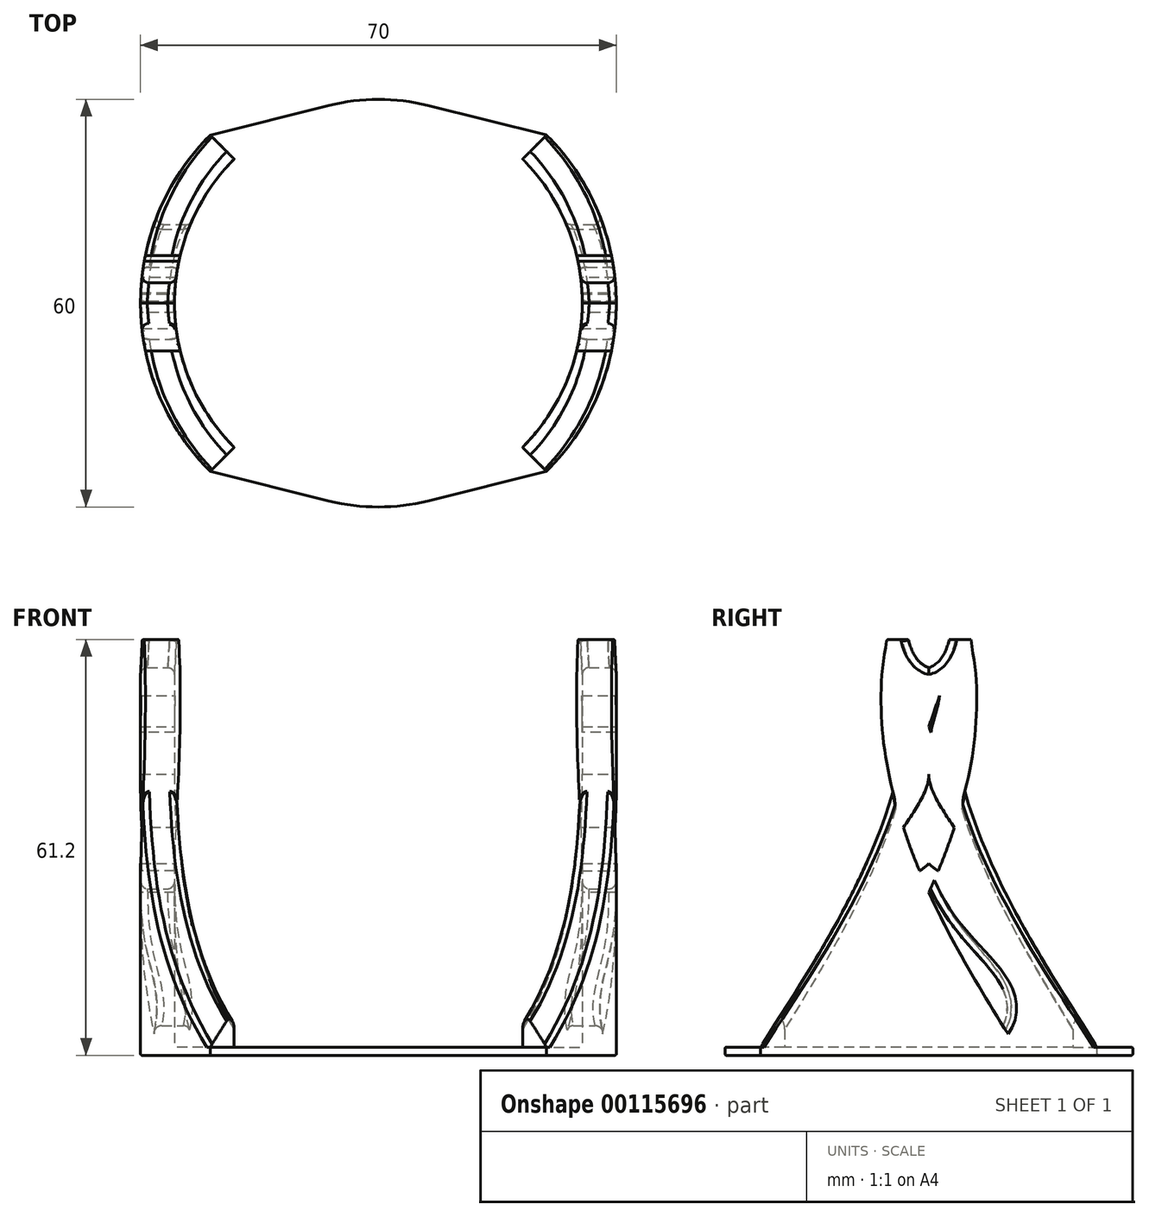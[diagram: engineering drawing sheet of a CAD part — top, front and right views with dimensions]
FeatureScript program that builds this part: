
annotation { "Feature Type Name" : "Feature", "Feature Type Description" : "" }
export const myFeature = defineFeature(function(context is Context, id is Id, definition is map)
    precondition{}
    {
        {
            var Q0;
            Q0=qCreatedBy(makeId("Top.planeOp"),FACE);
            var sketch = newSketch(context, id + "F0", { "sketchPlane" : qUnion([Q0])});
            skCircle(sketch, "E0", {"center": v(0, 0) * mm, "radius": 30 * mm});
            skArc(sketch, "E1", {"start": v(-24.75, 24.75) * mm, "mid": v(-35, 0) * mm, "end": v(-24.75, -24.75) * mm});
            skLineSegment(sketch, "E2", {"start": v(-21.21, 21.21) * mm, "end": v(-24.75, 24.75) * mm});
            skLineSegment(sketch, "E3.MirrorCS", {"start": v(-21.21, -21.21) * mm, "end": v(-24.75, -24.75) * mm});
            skLineSegment(sketch, "E4.MirrorCS", {"start": v(21.21, 21.21) * mm, "end": v(24.75, 24.75) * mm});
            skLineSegment(sketch, "E5.MirrorCS", {"start": v(21.21, -21.21) * mm, "end": v(24.75, -24.75) * mm});
            skArc(sketch, "E6.trimOffspring", {"start": v(24.75, -24.75) * mm, "mid": v(35, 0) * mm, "end": v(24.75, 24.75) * mm});
            skPoint(sketch, "E7.start.orphan", {"position": v(-35, 0) * mm});
            skLineSegment(sketch, "E8", {"start": v(-24.75, 24.75) * mm, "end": v(-7.26, 29.1) * mm});
            skLineSegment(sketch, "E9.MirrorCS", {"start": v(-24.75, -24.75) * mm, "end": v(-7.26, -29.1) * mm});
            skLineSegment(sketch, "E10.MirrorCS", {"start": v(24.75, 24.75) * mm, "end": v(7.26, 29.1) * mm});
            skLineSegment(sketch, "E11.MirrorCS", {"start": v(24.75, -24.75) * mm, "end": v(7.26, -29.1) * mm});
            skSolve(sketch);
        }
        {
            var Q0;
            {var subQ0=sQuery(id+"F0.wireOp",EDGE,"E0");var subQ1=makeQuery(id+"F0.imprint","INTERSECT",VERTEX,{"derivedFrom":[subQ0,sQuery(id+"F0.wireOp",EDGE,"E2")]});Q0=makeQuery(id+"F0.imprint","IMPRINT",FACE,{"disambiguationData":[TD([[makeQuery(id+"F0.imprint","IMPRINT",EDGE,{"disambiguationData":[TD([[subQ1,1.0]])],"derivedFrom":subQ0}),1.0]])]});}
            var Q1;
            {var subQ0=sQuery(id+"F0.wireOp",EDGE,"E2");Q1=makeQuery(id+"F0.imprint","IMPRINT",FACE,{"disambiguationData":[TD([[makeQuery(id+"F0.imprint","IMPRINT",EDGE,{"derivedFrom":subQ0}),-1.0]])]});}
            var Q2;
            {var subQ0=sQuery(id+"F0.wireOp",EDGE,"E4.MirrorCS");Q2=makeQuery(id+"F0.imprint","IMPRINT",FACE,{"disambiguationData":[TD([[makeQuery(id+"F0.imprint","IMPRINT",EDGE,{"derivedFrom":subQ0}),1.0]])]});}
            var Q3;
            {var subQ0=sQuery(id+"F0.wireOp",EDGE,"E5.MirrorCS");Q3=makeQuery(id+"F0.imprint","IMPRINT",FACE,{"disambiguationData":[TD([[makeQuery(id+"F0.imprint","IMPRINT",EDGE,{"derivedFrom":subQ0}),-1.0]])]});}
            var Q4;
            {var subQ0=sQuery(id+"F0.wireOp",EDGE,"E3.MirrorCS");Q4=makeQuery(id+"F0.imprint","IMPRINT",FACE,{"disambiguationData":[TD([[makeQuery(id+"F0.imprint","IMPRINT",EDGE,{"derivedFrom":subQ0}),1.0]])]});}
            extrude(context, id + "F1", {"entities" : qUnion([Q0, Q1, Q2, Q3, Q4]), "oppositeDirection" : true, "depth" : 1.2 * mm});
        }
        {
            var Q0;
            Q0=makeQuery(id+"F0.imprint","IMPRINT",FACE,{"disambiguationData":[TD([[makeQuery(id+"F0.imprint","IMPRINT",EDGE,{"derivedFrom":sQuery(id+"F0.wireOp",EDGE,"E1")}),1.0]])]});
            var Q1;
            {var subQ0=sQuery(id+"F0.wireOp",EDGE,"E4.MirrorCS");Q1=makeQuery(id+"F0.imprint","IMPRINT",FACE,{"disambiguationData":[TD([[makeQuery(id+"F0.imprint","IMPRINT",EDGE,{"derivedFrom":subQ0}),-1.0]])]});}
            extrude(context, id + "F2", {"entities" : qUnion([Q0, Q1]), "operationType" : NewBodyOperationType.ADD, "oppositeDirection" : true, "depth" : 1.2 * mm});
        }
        {
            var Q0;
            Q0=makeQuery(id+"F0.imprint","IMPRINT",FACE,{"disambiguationData":[TD([[makeQuery(id+"F0.imprint","IMPRINT",EDGE,{"derivedFrom":sQuery(id+"F0.wireOp",EDGE,"E1")}),1.0]])]});
            var Q1;
            {var subQ0=sQuery(id+"F0.wireOp",EDGE,"E4.MirrorCS");Q1=makeQuery(id+"F0.imprint","IMPRINT",FACE,{"disambiguationData":[TD([[makeQuery(id+"F0.imprint","IMPRINT",EDGE,{"derivedFrom":subQ0}),-1.0]])]});}
            extrude(context, id + "F3", {"entities" : qUnion([Q0, Q1]), "operationType" : NewBodyOperationType.ADD, "depth" : 60 * mm});
        }
        {
            var Q0;
            Q0=qCreatedBy(makeId("Right.planeOp"),FACE);
            var sketch = newSketch(context, id + "F4", { "sketchPlane" : qUnion([Q0])});
            skLineSegment(sketch, "E12.0", {"start": v(24.75, 60) * mm, "end": v(-24.75, 60) * mm});
            skLineSegment(sketch, "E13.0", {"start": v(24.75, 60) * mm, "end": v(24.75, 0) * mm});
            skLineSegment(sketch, "E14.0", {"start": v(-24.75, 60) * mm, "end": v(-24.75, 0) * mm});
            skFitSpline(sketch, "E15", {"points": [v(24.75, 0) * mm, v(4, 60) * mm], "startDerivative": vector(-24.66, 39.95) * mm, "endDerivative": vector(14.64, 68.11) * mm});
            skFitSpline(sketch, "E16.MirrorCS", {"points": [v(-24.75, 0) * mm, v(-4, 60) * mm], "startDerivative": vector(24.66, 39.95) * mm, "endDerivative": vector(-14.64, 68.11) * mm});
            skFitSpline(sketch, "E17.trimOffspring", {"points": [v(-16.24, -5.25) * mm, v(-15.27, -3.69) * mm, v(-12.96, -0.07) * mm, v(-8.84, 6.46) * mm, v(-4.47, 13.94) * mm, v(-0.26, 22.22) * mm, v(3.39, 31.24) * mm, v(6.05, 40.95) * mm, v(7, 49.56) * mm, v(6.72, 56.69) * mm, v(6.16, 60.3) * mm, v(5.78, 62.1) * mm, v(-16.24, -5.25) * mm]});
            skFitSpline(sketch, "E18.trimOffspring", {"points": [v(16.24, -5.25) * mm, v(15.27, -3.69) * mm, v(12.96, -0.07) * mm, v(8.84, 6.46) * mm, v(4.47, 13.94) * mm, v(0.26, 22.22) * mm, v(-3.39, 31.24) * mm, v(-6.05, 40.95) * mm, v(-7, 49.56) * mm, v(-6.72, 56.69) * mm, v(-6.16, 60.3) * mm, v(-5.78, 62.1) * mm, v(16.24, -5.25) * mm]});
            skFitSpline(sketch, "E19.trimOffspring", {"points": [v(16.24, -5.25) * mm, v(15.27, -3.69) * mm, v(12.96, -0.07) * mm, v(8.84, 6.46) * mm, v(4.47, 13.94) * mm, v(0.26, 22.22) * mm, v(-3.39, 31.24) * mm, v(-6.05, 40.95) * mm, v(-7, 49.56) * mm, v(-6.72, 56.69) * mm, v(-6.16, 60.3) * mm, v(-5.78, 62.1) * mm, v(16.24, -5.25) * mm]});
            skFitSpline(sketch, "E20.trimOffspring", {"points": [v(-16.24, -5.25) * mm, v(-15.27, -3.69) * mm, v(-12.96, -0.07) * mm, v(-8.84, 6.46) * mm, v(-4.47, 13.94) * mm, v(-0.26, 22.22) * mm, v(3.39, 31.24) * mm, v(6.05, 40.95) * mm, v(7, 49.56) * mm, v(6.72, 56.69) * mm, v(6.16, 60.3) * mm, v(5.78, 62.1) * mm, v(-16.24, -5.25) * mm]});
            skPoint(sketch, "E21.visualSharp", {"position": v(0, 27.02) * mm});
            skLineSegment(sketch, "E22", {"start": v(24.75, 0) * mm, "end": v(-24.75, 0) * mm});
            skLineSegment(sketch, "E23", {"start": v(6.2, 0.5) * mm, "end": v(0, 0.5) * mm});
            skPoint(sketch, "E24.visualSharp", {"position": v(12.54, 0.5) * mm});
            skLineSegment(sketch, "E25.MirrorCS", {"start": v(-6.2, 0.5) * mm, "end": v(0, 0.5) * mm});
            skFitSpline(sketch, "E26", {"points": [v(3, 60) * mm, v(0, 55.86) * mm], "startDerivative": vector(-2.3, -9.9) * mm, "endDerivative": vector(-1.7, -0.5) * mm});
            skFitSpline(sketch, "E27.MirrorCS", {"points": [v(-3, 60) * mm, v(0, 55.86) * mm], "startDerivative": vector(2.3, -9.9) * mm, "endDerivative": vector(1.7, -0.5) * mm});
            skFitSpline(sketch, "E28", {"points": [v(0, 52.84) * mm, v(0, 45.08) * mm], "startDerivative": vector(9.92, 7.33) * mm, "endDerivative": vector(-1.99, -10.58) * mm});
            skFitSpline(sketch, "E29", {"points": [v(0, 40.2) * mm, v(5.75, 27.7) * mm, v(0, 27.02) * mm], "startDerivative": vector(0, -21.2) * mm, "endDerivative": vector(-24.95, 23.94) * mm});
            skFitSpline(sketch, "E30.MirrorCS", {"points": [v(0, 52.84) * mm, v(0, 45.08) * mm], "startDerivative": vector(-9.92, 7.33) * mm, "endDerivative": vector(1.99, -10.58) * mm});
            skFitSpline(sketch, "E31.MirrorCS", {"points": [v(0, 40.2) * mm, v(-5.75, 27.7) * mm, v(0, 27.02) * mm], "startDerivative": vector(0, -21.2) * mm, "endDerivative": vector(24.95, 23.94) * mm});
            skFitSpline(sketch, "E32", {"points": [v(0, 23.84) * mm, v(11.42, 6.97) * mm, v(0, 2.63) * mm], "startDerivative": vector(19.77, -45.42) * mm, "endDerivative": vector(-65.43, 29.07) * mm});
            skFitSpline(sketch, "E33.MirrorCS", {"points": [v(0, 23.84) * mm, v(-11.42, 6.97) * mm, v(0, 2.63) * mm], "startDerivative": vector(-19.77, -45.42) * mm, "endDerivative": vector(65.43, 29.07) * mm});
            skSolve(sketch);
        }
        {
            var Q0;
            {var subQ0=sQuery(id+"F4.wireOp",EDGE,"E14.0");Q0=makeQuery(id+"F4.imprint","IMPRINT",FACE,{"disambiguationData":[TD([[makeQuery(id+"F4.imprint","IMPRINT",EDGE,{"derivedFrom":subQ0}),1.0]])]});}
            var Q1;
            {var subQ0=sQuery(id+"F4.wireOp",EDGE,"E13.0");Q1=makeQuery(id+"F4.imprint","IMPRINT",FACE,{"disambiguationData":[TD([[makeQuery(id+"F4.imprint","IMPRINT",EDGE,{"derivedFrom":subQ0}),-1.0]])]});}
            var Q2;
            Q2=makeQuery(id+"F4.imprint","IMPRINT",FACE,{"disambiguationData":[TD([[makeQuery(id+"F4.imprint","IMPRINT",EDGE,{"derivedFrom":sQuery(id+"F4.wireOp",EDGE,"OLSyuzr6-r6Sz-iabG-22gY-yzPiiR23RSYU")}),-1.0]])]});
            var Q3;
            {var subQ0=sQuery(id+"F4.wireOp",EDGE,"E26");Q3=makeQuery(id+"F4.imprint","IMPRINT",FACE,{"disambiguationData":[TD([[makeQuery(id+"F4.imprint","IMPRINT",EDGE,{"derivedFrom":subQ0}),-1.0]])]});}
            var Q4;
            Q4=makeQuery(id+"F4.imprint","IMPRINT",FACE,{"disambiguationData":[TD([[makeQuery(id+"F4.imprint","IMPRINT",EDGE,{"derivedFrom":sQuery(id+"F4.wireOp",EDGE,"E28")}),-1.0]])]});
            var Q5;
            Q5=makeQuery(id+"F4.imprint","IMPRINT",FACE,{"disambiguationData":[TD([[makeQuery(id+"F4.imprint","IMPRINT",EDGE,{"derivedFrom":sQuery(id+"F4.wireOp",EDGE,"E29")}),-1.0]])]});
            var Q6;
            Q6=makeQuery(id+"F4.imprint","IMPRINT",FACE,{"disambiguationData":[TD([[makeQuery(id+"F4.imprint","IMPRINT",EDGE,{"derivedFrom":sQuery(id+"F4.wireOp",EDGE,"E24.filletArc")}),1.0]])]});
            var Q7;
            Q7=makeQuery(id+"F4.imprint","IMPRINT",FACE,{"disambiguationData":[TD([[makeQuery(id+"F4.imprint","IMPRINT",EDGE,{"derivedFrom":sQuery(id+"F4.wireOp",EDGE,"E32")}),-1.0]])]});
            extrude(context, id + "F5", {"entities" : qUnion([Q0, Q1, Q2, Q3, Q4, Q5, Q6, Q7]), "operationType" : NewBodyOperationType.REMOVE, "endBound" : BoundingType.SYMMETRIC, "oppositeDirection" : true, "depth" : 80 * mm});
        }
        {
            var Q0;
            {var subQ0=sQuery(id+"F0.wireOp",EDGE,"E6.trimOffspring");Q0=makeQuery(id+"F5.boolean.opBoolean","INTERSECT",EDGE,{"derivedFrom":[makeQuery(id+"F3.boolean.opBoolean","MERGE",FACE,{"derivedFrom":[makeQuery(id+"F2.opExtrude","SWEPT_FACE",FACE,{"disambiguationData":[OSD([subQ0])]}),makeQuery(id+"F3.opExtrude","SWEPT_FACE",FACE,{"disambiguationData":[OSD([subQ0])]})]}),makeQuery(id+"F5.opExtrude","SWEPT_FACE",FACE,{"disambiguationData":[OSD([sQuery(id+"F4.wireOp",EDGE,"E15")])]})]});}
            var Q1;
            {var subQ0=sQuery(id+"F0.wireOp",EDGE,"E1");Q1=makeQuery(id+"F5.boolean.opBoolean","INTERSECT",EDGE,{"derivedFrom":[makeQuery(id+"F3.boolean.opBoolean","MERGE",FACE,{"derivedFrom":[makeQuery(id+"F2.opExtrude","SWEPT_FACE",FACE,{"disambiguationData":[OSD([subQ0])]}),makeQuery(id+"F3.opExtrude","SWEPT_FACE",FACE,{"disambiguationData":[OSD([subQ0])]})]}),makeQuery(id+"F5.opExtrude","SWEPT_FACE",FACE,{"disambiguationData":[OSD([sQuery(id+"F4.wireOp",EDGE,"E15")])]})]});}
            var Q2;
            {var subQ0=sQuery(id+"F0.wireOp",EDGE,"E0");Q2=makeQuery(id+"F5.boolean.opBoolean","INTERSECT",EDGE,{"derivedFrom":[makeQuery(id+"F3.opExtrude","SWEPT_FACE",FACE,{"disambiguationData":[OSD([subQ0]),TDD([makeQuery(id+"F0.imprint","IMPRINT",EDGE,{"disambiguationData":[TD([[makeQuery(id+"F0.imprint","INTERSECT",VERTEX,{"derivedFrom":[subQ0,sQuery(id+"F0.wireOp",EDGE,"E2")]}),-1.0]])],"derivedFrom":subQ0})])]}),makeQuery(id+"F5.opExtrude","SWEPT_FACE",FACE,{"disambiguationData":[OSD([sQuery(id+"F4.wireOp",EDGE,"E15")])]})]});}
            var Q3;
            {var subQ0=sQuery(id+"F0.wireOp",EDGE,"E0");Q3=makeQuery(id+"F5.boolean.opBoolean","INTERSECT",EDGE,{"derivedFrom":[makeQuery(id+"F3.opExtrude","SWEPT_FACE",FACE,{"disambiguationData":[OSD([subQ0]),TDD([makeQuery(id+"F0.imprint","IMPRINT",EDGE,{"disambiguationData":[TD([[makeQuery(id+"F0.imprint","INTERSECT",VERTEX,{"derivedFrom":[subQ0,sQuery(id+"F0.wireOp",EDGE,"E4.MirrorCS")]}),1.0]])],"derivedFrom":subQ0})])]}),makeQuery(id+"F5.opExtrude","SWEPT_FACE",FACE,{"disambiguationData":[OSD([sQuery(id+"F4.wireOp",EDGE,"E15")])]})]});}
            var Q4;
            {var subQ0=sQuery(id+"F0.wireOp",EDGE,"E6.trimOffspring");Q4=makeQuery(id+"F5.boolean.opBoolean","INTERSECT",EDGE,{"derivedFrom":[makeQuery(id+"F3.boolean.opBoolean","MERGE",FACE,{"derivedFrom":[makeQuery(id+"F2.opExtrude","SWEPT_FACE",FACE,{"disambiguationData":[OSD([subQ0])]}),makeQuery(id+"F3.opExtrude","SWEPT_FACE",FACE,{"disambiguationData":[OSD([subQ0])]})]}),makeQuery(id+"F5.opExtrude","SWEPT_FACE",FACE,{"disambiguationData":[OSD([sQuery(id+"F4.wireOp",EDGE,"E16.MirrorCS")])]})]});}
            var Q5;
            {var subQ0=sQuery(id+"F0.wireOp",EDGE,"E0");Q5=makeQuery(id+"F5.boolean.opBoolean","INTERSECT",EDGE,{"derivedFrom":[makeQuery(id+"F3.opExtrude","SWEPT_FACE",FACE,{"disambiguationData":[OSD([subQ0]),TDD([makeQuery(id+"F0.imprint","IMPRINT",EDGE,{"disambiguationData":[TD([[makeQuery(id+"F0.imprint","INTERSECT",VERTEX,{"derivedFrom":[subQ0,sQuery(id+"F0.wireOp",EDGE,"E4.MirrorCS")]}),1.0]])],"derivedFrom":subQ0})])]}),makeQuery(id+"F5.opExtrude","SWEPT_FACE",FACE,{"disambiguationData":[OSD([sQuery(id+"F4.wireOp",EDGE,"E16.MirrorCS")])]})]});}
            var Q6;
            {var subQ0=sQuery(id+"F0.wireOp",EDGE,"E1");Q6=makeQuery(id+"F5.boolean.opBoolean","INTERSECT",EDGE,{"derivedFrom":[makeQuery(id+"F3.boolean.opBoolean","MERGE",FACE,{"derivedFrom":[makeQuery(id+"F2.opExtrude","SWEPT_FACE",FACE,{"disambiguationData":[OSD([subQ0])]}),makeQuery(id+"F3.opExtrude","SWEPT_FACE",FACE,{"disambiguationData":[OSD([subQ0])]})]}),makeQuery(id+"F5.opExtrude","SWEPT_FACE",FACE,{"disambiguationData":[OSD([sQuery(id+"F4.wireOp",EDGE,"E16.MirrorCS")])]})]});}
            var Q7;
            {var subQ0=sQuery(id+"F0.wireOp",EDGE,"E0");Q7=makeQuery(id+"F5.boolean.opBoolean","INTERSECT",EDGE,{"derivedFrom":[makeQuery(id+"F3.opExtrude","SWEPT_FACE",FACE,{"disambiguationData":[OSD([subQ0]),TDD([makeQuery(id+"F0.imprint","IMPRINT",EDGE,{"disambiguationData":[TD([[makeQuery(id+"F0.imprint","INTERSECT",VERTEX,{"derivedFrom":[subQ0,sQuery(id+"F0.wireOp",EDGE,"E2")]}),-1.0]])],"derivedFrom":subQ0})])]}),makeQuery(id+"F5.opExtrude","SWEPT_FACE",FACE,{"disambiguationData":[OSD([sQuery(id+"F4.wireOp",EDGE,"E16.MirrorCS")])]})]});}
            var Q8;
            {var subQ0=sQuery(id+"F0.wireOp",EDGE,"E1");Q8=makeQuery(id+"F5.boolean.opBoolean","INTERSECT",EDGE,{"derivedFrom":[makeQuery(id+"F3.boolean.opBoolean","MERGE",FACE,{"derivedFrom":[makeQuery(id+"F2.opExtrude","SWEPT_FACE",FACE,{"disambiguationData":[OSD([subQ0])]}),makeQuery(id+"F3.opExtrude","SWEPT_FACE",FACE,{"disambiguationData":[OSD([subQ0])]})]}),makeQuery(id+"F5.opExtrude","SWEPT_FACE",FACE,{"disambiguationData":[OSD([sQuery(id+"F4.wireOp",EDGE,"E32")])]})]});}
            var Q9;
            {var subQ0=sQuery(id+"F0.wireOp",EDGE,"E1");Q9=makeQuery(id+"F5.boolean.opBoolean","INTERSECT",EDGE,{"derivedFrom":[makeQuery(id+"F3.boolean.opBoolean","MERGE",FACE,{"derivedFrom":[makeQuery(id+"F2.opExtrude","SWEPT_FACE",FACE,{"disambiguationData":[OSD([subQ0])]}),makeQuery(id+"F3.opExtrude","SWEPT_FACE",FACE,{"disambiguationData":[OSD([subQ0])]})]}),makeQuery(id+"F5.opExtrude","SWEPT_FACE",FACE,{"disambiguationData":[OSD([sQuery(id+"F4.wireOp",EDGE,"E33.MirrorCS")])]})]});}
            var Q10;
            {var subQ0=sQuery(id+"F0.wireOp",EDGE,"E0");Q10=makeQuery(id+"F5.boolean.opBoolean","INTERSECT",EDGE,{"derivedFrom":[makeQuery(id+"F3.opExtrude","SWEPT_FACE",FACE,{"disambiguationData":[OSD([subQ0]),TDD([makeQuery(id+"F0.imprint","IMPRINT",EDGE,{"disambiguationData":[TD([[makeQuery(id+"F0.imprint","INTERSECT",VERTEX,{"derivedFrom":[subQ0,sQuery(id+"F0.wireOp",EDGE,"E4.MirrorCS")]}),1.0]])],"derivedFrom":subQ0})])]}),makeQuery(id+"F5.opExtrude","SWEPT_FACE",FACE,{"disambiguationData":[OSD([sQuery(id+"F4.wireOp",EDGE,"E33.MirrorCS")])]})]});}
            var Q11;
            {var subQ0=sQuery(id+"F0.wireOp",EDGE,"E0");Q11=makeQuery(id+"F5.boolean.opBoolean","INTERSECT",EDGE,{"derivedFrom":[makeQuery(id+"F3.opExtrude","SWEPT_FACE",FACE,{"disambiguationData":[OSD([subQ0]),TDD([makeQuery(id+"F0.imprint","IMPRINT",EDGE,{"disambiguationData":[TD([[makeQuery(id+"F0.imprint","INTERSECT",VERTEX,{"derivedFrom":[subQ0,sQuery(id+"F0.wireOp",EDGE,"E4.MirrorCS")]}),1.0]])],"derivedFrom":subQ0})])]}),makeQuery(id+"F5.opExtrude","SWEPT_FACE",FACE,{"disambiguationData":[OSD([sQuery(id+"F4.wireOp",EDGE,"E32")])]})]});}
            var Q12;
            {var subQ0=sQuery(id+"F0.wireOp",EDGE,"E6.trimOffspring");Q12=makeQuery(id+"F5.boolean.opBoolean","INTERSECT",EDGE,{"derivedFrom":[makeQuery(id+"F3.boolean.opBoolean","MERGE",FACE,{"derivedFrom":[makeQuery(id+"F2.opExtrude","SWEPT_FACE",FACE,{"disambiguationData":[OSD([subQ0])]}),makeQuery(id+"F3.opExtrude","SWEPT_FACE",FACE,{"disambiguationData":[OSD([subQ0])]})]}),makeQuery(id+"F5.opExtrude","SWEPT_FACE",FACE,{"disambiguationData":[OSD([sQuery(id+"F4.wireOp",EDGE,"E32")])]})]});}
            var Q13;
            {var subQ0=sQuery(id+"F0.wireOp",EDGE,"E0");Q13=makeQuery(id+"F5.boolean.opBoolean","INTERSECT",EDGE,{"derivedFrom":[makeQuery(id+"F3.opExtrude","SWEPT_FACE",FACE,{"disambiguationData":[OSD([subQ0]),TDD([makeQuery(id+"F0.imprint","IMPRINT",EDGE,{"disambiguationData":[TD([[makeQuery(id+"F0.imprint","INTERSECT",VERTEX,{"derivedFrom":[subQ0,sQuery(id+"F0.wireOp",EDGE,"E2")]}),-1.0]])],"derivedFrom":subQ0})])]}),makeQuery(id+"F5.opExtrude","SWEPT_FACE",FACE,{"disambiguationData":[OSD([sQuery(id+"F4.wireOp",EDGE,"E32")])]})]});}
            var Q14;
            {var subQ0=sQuery(id+"F0.wireOp",EDGE,"E0");Q14=makeQuery(id+"F5.boolean.opBoolean","INTERSECT",EDGE,{"derivedFrom":[makeQuery(id+"F3.opExtrude","SWEPT_FACE",FACE,{"disambiguationData":[OSD([subQ0]),TDD([makeQuery(id+"F0.imprint","IMPRINT",EDGE,{"disambiguationData":[TD([[makeQuery(id+"F0.imprint","INTERSECT",VERTEX,{"derivedFrom":[subQ0,sQuery(id+"F0.wireOp",EDGE,"E2")]}),-1.0]])],"derivedFrom":subQ0})])]}),makeQuery(id+"F5.opExtrude","SWEPT_FACE",FACE,{"disambiguationData":[OSD([sQuery(id+"F4.wireOp",EDGE,"E33.MirrorCS")])]})]});}
            var Q15;
            {var subQ0=sQuery(id+"F0.wireOp",EDGE,"E6.trimOffspring");Q15=makeQuery(id+"F5.boolean.opBoolean","INTERSECT",EDGE,{"derivedFrom":[makeQuery(id+"F3.boolean.opBoolean","MERGE",FACE,{"derivedFrom":[makeQuery(id+"F2.opExtrude","SWEPT_FACE",FACE,{"disambiguationData":[OSD([subQ0])]}),makeQuery(id+"F3.opExtrude","SWEPT_FACE",FACE,{"disambiguationData":[OSD([subQ0])]})]}),makeQuery(id+"F5.opExtrude","SWEPT_FACE",FACE,{"disambiguationData":[OSD([sQuery(id+"F4.wireOp",EDGE,"E33.MirrorCS")])]})]});}
            var Q16;
            {var subQ0=sQuery(id+"F0.wireOp",EDGE,"E6.trimOffspring");Q16=makeQuery(id+"F5.boolean.opBoolean","INTERSECT",EDGE,{"derivedFrom":[makeQuery(id+"F3.boolean.opBoolean","MERGE",FACE,{"derivedFrom":[makeQuery(id+"F2.opExtrude","SWEPT_FACE",FACE,{"disambiguationData":[OSD([subQ0])]}),makeQuery(id+"F3.opExtrude","SWEPT_FACE",FACE,{"disambiguationData":[OSD([subQ0])]})]}),makeQuery(id+"F5.opExtrude","SWEPT_FACE",FACE,{"disambiguationData":[OSD([sQuery(id+"F4.wireOp",EDGE,"E27.MirrorCS")])]})]});}
            var Q17;
            {var subQ0=sQuery(id+"F0.wireOp",EDGE,"E0");Q17=makeQuery(id+"F5.boolean.opBoolean","INTERSECT",EDGE,{"derivedFrom":[makeQuery(id+"F3.opExtrude","SWEPT_FACE",FACE,{"disambiguationData":[OSD([subQ0]),TDD([makeQuery(id+"F0.imprint","IMPRINT",EDGE,{"disambiguationData":[TD([[makeQuery(id+"F0.imprint","INTERSECT",VERTEX,{"derivedFrom":[subQ0,sQuery(id+"F0.wireOp",EDGE,"E4.MirrorCS")]}),1.0]])],"derivedFrom":subQ0})])]}),makeQuery(id+"F5.opExtrude","SWEPT_FACE",FACE,{"disambiguationData":[OSD([sQuery(id+"F4.wireOp",EDGE,"E26")])]})]});}
            var Q18;
            {var subQ0=sQuery(id+"F0.wireOp",EDGE,"E0");Q18=makeQuery(id+"F5.boolean.opBoolean","INTERSECT",EDGE,{"derivedFrom":[makeQuery(id+"F3.opExtrude","SWEPT_FACE",FACE,{"disambiguationData":[OSD([subQ0]),TDD([makeQuery(id+"F0.imprint","IMPRINT",EDGE,{"disambiguationData":[TD([[makeQuery(id+"F0.imprint","INTERSECT",VERTEX,{"derivedFrom":[subQ0,sQuery(id+"F0.wireOp",EDGE,"E4.MirrorCS")]}),1.0]])],"derivedFrom":subQ0})])]}),makeQuery(id+"F5.opExtrude","SWEPT_FACE",FACE,{"disambiguationData":[OSD([sQuery(id+"F4.wireOp",EDGE,"E27.MirrorCS")])]})]});}
            var Q19;
            {var subQ0=sQuery(id+"F0.wireOp",EDGE,"E6.trimOffspring");Q19=makeQuery(id+"F5.boolean.opBoolean","INTERSECT",EDGE,{"derivedFrom":[makeQuery(id+"F3.boolean.opBoolean","MERGE",FACE,{"derivedFrom":[makeQuery(id+"F2.opExtrude","SWEPT_FACE",FACE,{"disambiguationData":[OSD([subQ0])]}),makeQuery(id+"F3.opExtrude","SWEPT_FACE",FACE,{"disambiguationData":[OSD([subQ0])]})]}),makeQuery(id+"F5.opExtrude","SWEPT_FACE",FACE,{"disambiguationData":[OSD([sQuery(id+"F4.wireOp",EDGE,"E26")])]})]});}
            var Q20;
            {var subQ0=sQuery(id+"F0.wireOp",EDGE,"E0");Q20=makeQuery(id+"F5.boolean.opBoolean","INTERSECT",EDGE,{"derivedFrom":[makeQuery(id+"F3.opExtrude","SWEPT_FACE",FACE,{"disambiguationData":[OSD([subQ0]),TDD([makeQuery(id+"F0.imprint","IMPRINT",EDGE,{"disambiguationData":[TD([[makeQuery(id+"F0.imprint","INTERSECT",VERTEX,{"derivedFrom":[subQ0,sQuery(id+"F0.wireOp",EDGE,"E2")]}),-1.0]])],"derivedFrom":subQ0})])]}),makeQuery(id+"F5.opExtrude","SWEPT_FACE",FACE,{"disambiguationData":[OSD([sQuery(id+"F4.wireOp",EDGE,"E26")])]})]});}
            var Q21;
            {var subQ0=sQuery(id+"F0.wireOp",EDGE,"E1");Q21=makeQuery(id+"F5.boolean.opBoolean","INTERSECT",EDGE,{"derivedFrom":[makeQuery(id+"F3.boolean.opBoolean","MERGE",FACE,{"derivedFrom":[makeQuery(id+"F2.opExtrude","SWEPT_FACE",FACE,{"disambiguationData":[OSD([subQ0])]}),makeQuery(id+"F3.opExtrude","SWEPT_FACE",FACE,{"disambiguationData":[OSD([subQ0])]})]}),makeQuery(id+"F5.opExtrude","SWEPT_FACE",FACE,{"disambiguationData":[OSD([sQuery(id+"F4.wireOp",EDGE,"E26")])]})]});}
            var Q22;
            {var subQ0=sQuery(id+"F0.wireOp",EDGE,"E0");Q22=makeQuery(id+"F5.boolean.opBoolean","INTERSECT",EDGE,{"derivedFrom":[makeQuery(id+"F3.opExtrude","SWEPT_FACE",FACE,{"disambiguationData":[OSD([subQ0]),TDD([makeQuery(id+"F0.imprint","IMPRINT",EDGE,{"disambiguationData":[TD([[makeQuery(id+"F0.imprint","INTERSECT",VERTEX,{"derivedFrom":[subQ0,sQuery(id+"F0.wireOp",EDGE,"E2")]}),-1.0]])],"derivedFrom":subQ0})])]}),makeQuery(id+"F5.opExtrude","SWEPT_FACE",FACE,{"disambiguationData":[OSD([sQuery(id+"F4.wireOp",EDGE,"E27.MirrorCS")])]})]});}
            var Q23;
            {var subQ0=sQuery(id+"F0.wireOp",EDGE,"E1");Q23=makeQuery(id+"F5.boolean.opBoolean","INTERSECT",EDGE,{"derivedFrom":[makeQuery(id+"F3.boolean.opBoolean","MERGE",FACE,{"derivedFrom":[makeQuery(id+"F2.opExtrude","SWEPT_FACE",FACE,{"disambiguationData":[OSD([subQ0])]}),makeQuery(id+"F3.opExtrude","SWEPT_FACE",FACE,{"disambiguationData":[OSD([subQ0])]})]}),makeQuery(id+"F5.opExtrude","SWEPT_FACE",FACE,{"disambiguationData":[OSD([sQuery(id+"F4.wireOp",EDGE,"E27.MirrorCS")])]})]});}
            fillet(context, id + "F6", {"entities" : qUnion([Q0, Q1, Q2, Q3, Q4, Q5, Q6, Q7, Q8, Q9, Q10, Q11, Q12, Q13, Q14, Q15, Q16, Q17, Q18, Q19, Q20, Q21, Q22, Q23]), "radius" : 1 * mm, "tangentPropagation" : true, "allowEdgeOverflow" : false});
        }
        {
            var Q0;
            {var subQ0=sQuery(id+"F0.wireOp",EDGE,"E0");Q0=makeQuery(id+"F1.opExtrude","CAP_EDGE",EDGE,{"disambiguationData":[OSD([subQ0]),TDD([makeQuery(id+"F0.imprint","IMPRINT",EDGE,{"disambiguationData":[TD([[makeQuery(id+"F0.imprint","INTERSECT",VERTEX,{"derivedFrom":[subQ0,sQuery(id+"F0.wireOp",EDGE,"E9.MirrorCS")]}),-1.0]])],"derivedFrom":subQ0})])],"isStart":true});}
            var Q1;
            Q1=makeQuery(id+"F1.opExtrude","CAP_EDGE",EDGE,{"disambiguationData":[OSD([sQuery(id+"F0.wireOp",EDGE,"E11.MirrorCS")])],"isStart":false});
            var Q2;
            Q2=makeQuery(id+"F1.opExtrude","SWEPT_FACE",FACE,{"disambiguationData":[OSD([sQuery(id+"F0.wireOp",EDGE,"E10.MirrorCS")])]});
            var Q3;
            Q3=makeQuery(id+"F2.opExtrude","CAP_EDGE",EDGE,{"disambiguationData":[OSD([sQuery(id+"F0.wireOp",EDGE,"E6.trimOffspring")])],"isStart":false});
            var Q4;
            Q4=makeQuery(id+"F2.opExtrude","CAP_EDGE",EDGE,{"disambiguationData":[OSD([sQuery(id+"F0.wireOp",EDGE,"E1")])],"isStart":false});
            var Q5;
            Q5=makeQuery(id+"F5.boolean.opBoolean","COPY",EDGE,{"disambiguationData":[OD(1.0)],"derivedFrom":makeQuery(id+"F5.opExtrude","SWEPT_EDGE",EDGE,{"disambiguationData":[OSD([sQuery(id+"F4.wireOp",EDGE,"E12.0"),sQuery(id+"F4.wireOp",EDGE,"E26")])]})});
            var Q6;
            Q6=makeQuery(id+"F5.boolean.opBoolean","COPY",EDGE,{"disambiguationData":[OD(1.0)],"derivedFrom":makeQuery(id+"F5.opExtrude","SWEPT_EDGE",EDGE,{"disambiguationData":[OSD([sQuery(id+"F4.wireOp",EDGE,"E12.0"),sQuery(id+"F4.wireOp",EDGE,"E27.MirrorCS")])]})});
            var Q7;
            Q7=makeQuery(id+"F5.boolean.opBoolean","COPY",EDGE,{"disambiguationData":[OD(1.0)],"derivedFrom":makeQuery(id+"F5.opExtrude","SWEPT_EDGE",EDGE,{"disambiguationData":[OSD([sQuery(id+"F4.wireOp",EDGE,"E12.0"),sQuery(id+"F4.wireOp",EDGE,"E15")])]})});
            var Q8;
            Q8=makeQuery(id+"F5.boolean.opBoolean","COPY",EDGE,{"disambiguationData":[OD(0.0)],"derivedFrom":makeQuery(id+"F5.opExtrude","SWEPT_EDGE",EDGE,{"disambiguationData":[OSD([sQuery(id+"F4.wireOp",EDGE,"E12.0"),sQuery(id+"F4.wireOp",EDGE,"E15")])]})});
            var Q9;
            Q9=makeQuery(id+"F5.boolean.opBoolean","COPY",EDGE,{"disambiguationData":[OD(0.0)],"derivedFrom":makeQuery(id+"F5.opExtrude","SWEPT_EDGE",EDGE,{"disambiguationData":[OSD([sQuery(id+"F4.wireOp",EDGE,"E12.0"),sQuery(id+"F4.wireOp",EDGE,"E26")])]})});
            var Q10;
            Q10=makeQuery(id+"F5.boolean.opBoolean","COPY",EDGE,{"disambiguationData":[OD(0.0)],"derivedFrom":makeQuery(id+"F5.opExtrude","SWEPT_EDGE",EDGE,{"disambiguationData":[OSD([sQuery(id+"F4.wireOp",EDGE,"E12.0"),sQuery(id+"F4.wireOp",EDGE,"E27.MirrorCS")])]})});
            var Q11;
            Q11=makeQuery(id+"F5.boolean.opBoolean","COPY",EDGE,{"disambiguationData":[OD(0.0)],"derivedFrom":makeQuery(id+"F5.opExtrude","SWEPT_EDGE",EDGE,{"disambiguationData":[OSD([sQuery(id+"F4.wireOp",EDGE,"E12.0"),sQuery(id+"F4.wireOp",EDGE,"E16.MirrorCS")])]})});
            var Q12;
            Q12=makeQuery(id+"F5.boolean.opBoolean","COPY",EDGE,{"disambiguationData":[OD(1.0)],"derivedFrom":makeQuery(id+"F5.opExtrude","SWEPT_EDGE",EDGE,{"disambiguationData":[OSD([sQuery(id+"F4.wireOp",EDGE,"E12.0"),sQuery(id+"F4.wireOp",EDGE,"E16.MirrorCS")])]})});
            fillet(context, id + "F7", {"entities" : qUnion([Q0, Q1, Q2, Q3, Q4, Q5, Q6, Q7, Q8, Q9, Q10, Q11, Q12]), "radius" : 0.2 * mm, "tangentPropagation" : true, "allowEdgeOverflow" : false});
        }
    });
